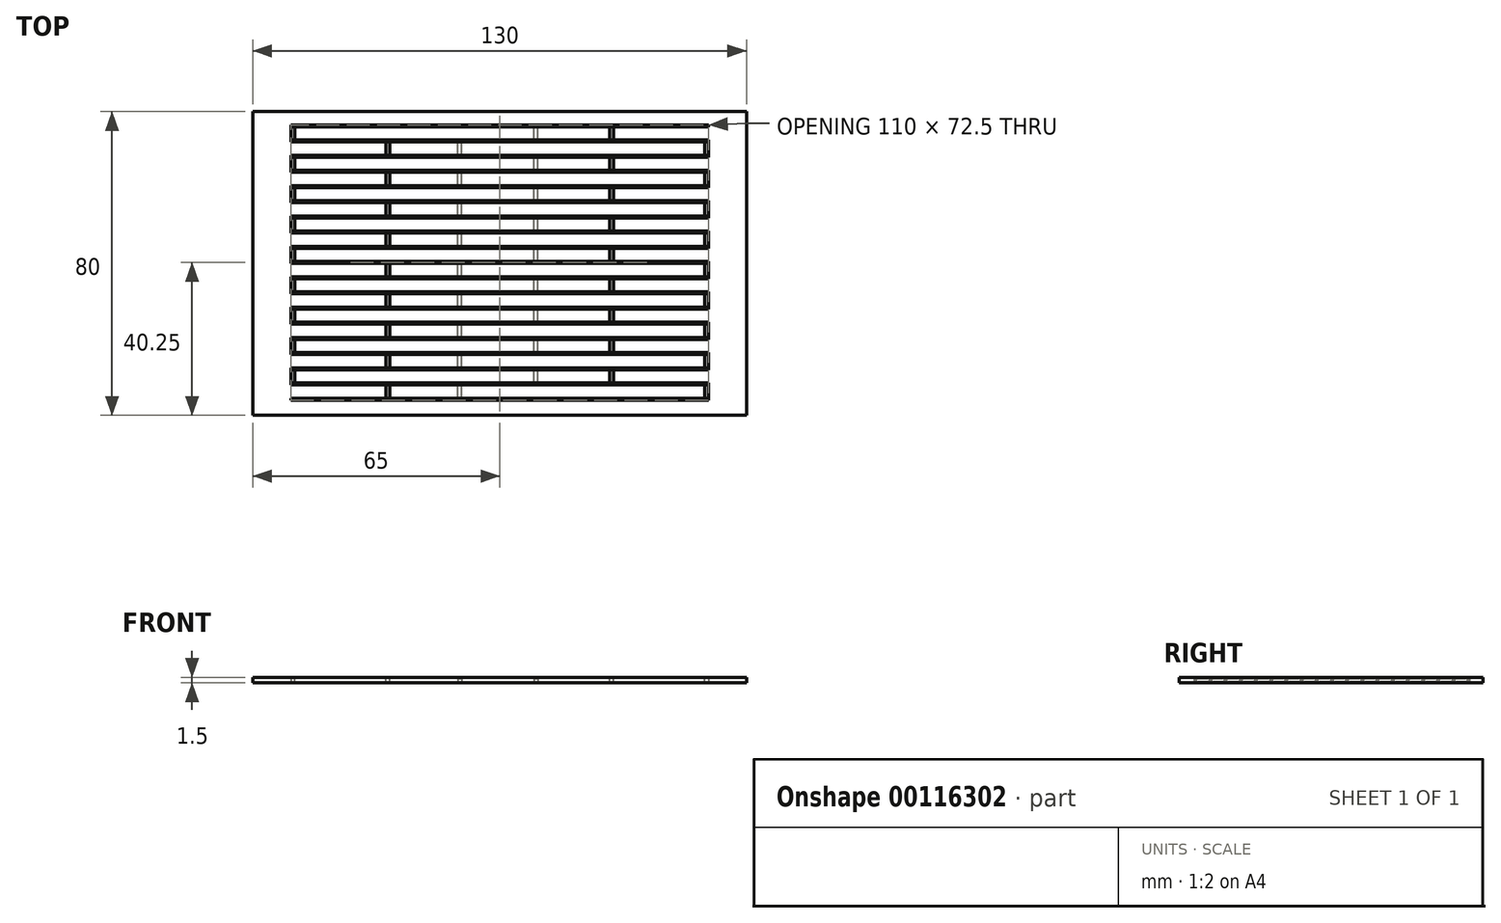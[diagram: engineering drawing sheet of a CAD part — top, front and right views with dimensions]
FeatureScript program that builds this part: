
annotation { "Feature Type Name" : "Feature", "Feature Type Description" : "" }
export const myFeature = defineFeature(function(context is Context, id is Id, definition is map)
    precondition{}
    {
        {
            var Q0;
            Q0=qCreatedBy(makeId("Top.planeOp"),FACE);
            var sketch = newSketch(context, id + "F0", { "sketchPlane" : qUnion([Q0])});
            skLineSegment(sketch, "E0.bottom", {"start": v(65, -40) * mm, "end": v(-65, -40) * mm});
            skLineSegment(sketch, "E0.top", {"start": v(65, 40) * mm, "end": v(-65, 40) * mm});
            skLineSegment(sketch, "E0.left", {"start": v(65, -40) * mm, "end": v(65, 40) * mm});
            skLineSegment(sketch, "E0.right", {"start": v(-65, -40) * mm, "end": v(-65, 40) * mm});
            skLineSegment(sketch, "E1", {"start": v(-55, 36.5) * mm, "end": v(-55, 36) * mm});
            skLineSegment(sketch, "E2.MirrorCS", {"start": v(55, 36.5) * mm, "end": v(55, 36) * mm});
            skLineSegment(sketch, "E3", {"start": v(-55, 36.5) * mm, "end": v(55, 36.5) * mm});
            skLineSegment(sketch, "E4", {"start": v(-55, 36) * mm, "end": v(55, 36) * mm});
            skLineSegment(sketch, "E5.0.1.0", {"start": v(-55, 32.5) * mm, "end": v(55, 32.5) * mm});
            skLineSegment(sketch, "E5.0.1.1", {"start": v(-55, 32) * mm, "end": v(55, 32) * mm});
            skLineSegment(sketch, "E5.0.2.0", {"start": v(-55, 28.5) * mm, "end": v(55, 28.5) * mm});
            skLineSegment(sketch, "E5.0.2.1", {"start": v(-55, 28) * mm, "end": v(55, 28) * mm});
            skLineSegment(sketch, "E5.0.3.0", {"start": v(-55, 24.5) * mm, "end": v(55, 24.5) * mm});
            skLineSegment(sketch, "E5.0.3.1", {"start": v(-55, 24) * mm, "end": v(55, 24) * mm});
            skLineSegment(sketch, "E5.0.4.0", {"start": v(-55, 20.5) * mm, "end": v(55, 20.5) * mm});
            skLineSegment(sketch, "E5.0.4.1", {"start": v(-55, 20) * mm, "end": v(55, 20) * mm});
            skLineSegment(sketch, "E5.0.5.0", {"start": v(-55, 16.5) * mm, "end": v(55, 16.5) * mm});
            skLineSegment(sketch, "E5.0.5.1", {"start": v(-55, 16) * mm, "end": v(55, 16) * mm});
            skLineSegment(sketch, "E5.0.6.0", {"start": v(-55, 12.5) * mm, "end": v(55, 12.5) * mm});
            skLineSegment(sketch, "E5.0.6.1", {"start": v(-55, 12) * mm, "end": v(55, 12) * mm});
            skLineSegment(sketch, "E5.0.7.0", {"start": v(-55, 8.5) * mm, "end": v(55, 8.5) * mm});
            skLineSegment(sketch, "E5.0.7.1", {"start": v(-55, 8) * mm, "end": v(55, 8) * mm});
            skLineSegment(sketch, "E5.0.8.0", {"start": v(-55, 4.5) * mm, "end": v(55, 4.5) * mm});
            skLineSegment(sketch, "E5.0.8.1", {"start": v(-55, 4) * mm, "end": v(55, 4) * mm});
            skLineSegment(sketch, "E5.0.9.0", {"start": v(-55, 0.5) * mm, "end": v(55, 0.5) * mm});
            skLineSegment(sketch, "E5.0.9.1", {"start": v(-55, 0) * mm, "end": v(55, 0) * mm});
            skLineSegment(sketch, "E5.0.10.0", {"start": v(-55, -3.5) * mm, "end": v(55, -3.5) * mm});
            skLineSegment(sketch, "E5.0.10.1", {"start": v(-55, -4) * mm, "end": v(55, -4) * mm});
            skLineSegment(sketch, "E5.0.11.0", {"start": v(-55, -7.5) * mm, "end": v(55, -7.5) * mm});
            skLineSegment(sketch, "E5.0.11.1", {"start": v(-55, -8) * mm, "end": v(55, -8) * mm});
            skLineSegment(sketch, "E5.0.12.0", {"start": v(-55, -11.5) * mm, "end": v(55, -11.5) * mm});
            skLineSegment(sketch, "E5.0.12.1", {"start": v(-55, -12) * mm, "end": v(55, -12) * mm});
            skLineSegment(sketch, "E5.0.13.0", {"start": v(-55, -15.5) * mm, "end": v(55, -15.5) * mm});
            skLineSegment(sketch, "E5.0.13.1", {"start": v(-55, -16) * mm, "end": v(55, -16) * mm});
            skLineSegment(sketch, "E5.0.14.0", {"start": v(-55, -19.5) * mm, "end": v(55, -19.5) * mm});
            skLineSegment(sketch, "E5.0.14.1", {"start": v(-55, -20) * mm, "end": v(55, -20) * mm});
            skLineSegment(sketch, "E5.0.15.0", {"start": v(-55, -23.5) * mm, "end": v(55, -23.5) * mm});
            skLineSegment(sketch, "E5.0.15.1", {"start": v(-55, -24) * mm, "end": v(55, -24) * mm});
            skLineSegment(sketch, "E5.0.16.0", {"start": v(-55, -27.5) * mm, "end": v(55, -27.5) * mm});
            skLineSegment(sketch, "E5.0.16.1", {"start": v(-55, -28) * mm, "end": v(55, -28) * mm});
            skLineSegment(sketch, "E5.0.17.0", {"start": v(-55, -31.5) * mm, "end": v(55, -31.5) * mm});
            skLineSegment(sketch, "E5.0.17.1", {"start": v(-55, -32) * mm, "end": v(55, -32) * mm});
            skLineSegment(sketch, "E5.0.18.0", {"start": v(-55, -35.5) * mm, "end": v(55, -35.5) * mm});
            skLineSegment(sketch, "E5.0.18.1", {"start": v(-55, -36) * mm, "end": v(55, -36) * mm});
            skLineSegment(sketch, "E5.direction1", {"start": v(-55, 36.5) * mm, "end": v(-12.48, 36.5) * mm, "construction": true});
            skLineSegment(sketch, "E5.direction2", {"start": v(-55, 36.5) * mm, "end": v(-55, 36) * mm, "construction": true});
            skPoint(sketch, "E6.orphan", {"position": v(-55, 40) * mm});
            skPoint(sketch, "E7.orphan", {"position": v(55, 40) * mm});
            skLineSegment(sketch, "E8.trimOffspring", {"start": v(55, 32.5) * mm, "end": v(55, 32) * mm});
            skLineSegment(sketch, "E9.trimOffspring", {"start": v(55, 28.5) * mm, "end": v(55, 28) * mm});
            skLineSegment(sketch, "E10.trimOffspring", {"start": v(55, 24.5) * mm, "end": v(55, 24) * mm});
            skLineSegment(sketch, "E11.trimOffspring", {"start": v(55, 20.5) * mm, "end": v(55, 20) * mm});
            skLineSegment(sketch, "E12.trimOffspring", {"start": v(55, 16.5) * mm, "end": v(55, 16) * mm});
            skLineSegment(sketch, "E13.trimOffspring", {"start": v(55, 12.5) * mm, "end": v(55, 12) * mm});
            skLineSegment(sketch, "E14.trimOffspring", {"start": v(55, 8.5) * mm, "end": v(55, 8) * mm});
            skLineSegment(sketch, "E15.trimOffspring", {"start": v(55, 4.5) * mm, "end": v(55, 4) * mm});
            skLineSegment(sketch, "E16.trimOffspring", {"start": v(55, 0.5) * mm, "end": v(55, 0) * mm});
            skLineSegment(sketch, "E17.trimOffspring", {"start": v(55, -3.5) * mm, "end": v(55, -4) * mm});
            skLineSegment(sketch, "E18.trimOffspring", {"start": v(55, -7.5) * mm, "end": v(55, -8) * mm});
            skLineSegment(sketch, "E19.trimOffspring", {"start": v(55, -11.5) * mm, "end": v(55, -12) * mm});
            skLineSegment(sketch, "E20.trimOffspring", {"start": v(55, -15.5) * mm, "end": v(55, -16) * mm});
            skLineSegment(sketch, "E21.trimOffspring", {"start": v(55, -19.5) * mm, "end": v(55, -20) * mm});
            skLineSegment(sketch, "E22.trimOffspring", {"start": v(55, -23.5) * mm, "end": v(55, -24) * mm});
            skLineSegment(sketch, "E23.trimOffspring", {"start": v(55, -27.5) * mm, "end": v(55, -28) * mm});
            skLineSegment(sketch, "E24.trimOffspring", {"start": v(55, -31.5) * mm, "end": v(55, -32) * mm});
            skLineSegment(sketch, "E25.trimOffspring", {"start": v(55, -35.5) * mm, "end": v(55, -36) * mm});
            skLineSegment(sketch, "E26.trimOffspring", {"start": v(-55, -31.5) * mm, "end": v(-55, -32) * mm});
            skLineSegment(sketch, "E27.trimOffspring", {"start": v(-55, -23.5) * mm, "end": v(-55, -24) * mm});
            skLineSegment(sketch, "E28.trimOffspring", {"start": v(-55, -15.5) * mm, "end": v(-55, -16) * mm});
            skLineSegment(sketch, "E29.trimOffspring", {"start": v(-55, -11.5) * mm, "end": v(-55, -12) * mm});
            skLineSegment(sketch, "E30.trimOffspring", {"start": v(-55, -7.5) * mm, "end": v(-55, -8) * mm});
            skLineSegment(sketch, "E31.trimOffspring", {"start": v(-55, -3.5) * mm, "end": v(-55, -4) * mm});
            skLineSegment(sketch, "E32.trimOffspring", {"start": v(-55, 0.5) * mm, "end": v(-55, 0) * mm});
            skLineSegment(sketch, "E33.trimOffspring", {"start": v(-55, 4.5) * mm, "end": v(-55, 4) * mm});
            skLineSegment(sketch, "E34.trimOffspring", {"start": v(-55, 8.5) * mm, "end": v(-55, 8) * mm});
            skLineSegment(sketch, "E35.trimOffspring", {"start": v(-55, 12.5) * mm, "end": v(-55, 12) * mm});
            skLineSegment(sketch, "E36.trimOffspring", {"start": v(-55, 16.5) * mm, "end": v(-55, 16) * mm});
            skLineSegment(sketch, "E37.trimOffspring", {"start": v(-55, -27.5) * mm, "end": v(-55, -28) * mm});
            skLineSegment(sketch, "E38.trimOffspring", {"start": v(-55, -19.5) * mm, "end": v(-55, -20) * mm});
            skLineSegment(sketch, "E39.trimOffspring", {"start": v(-55, -35.5) * mm, "end": v(-55, -36) * mm});
            skPoint(sketch, "E40.orphan", {"position": v(-55, -40) * mm});
            skLineSegment(sketch, "E41.trimOffspring", {"start": v(-55, 24.5) * mm, "end": v(-55, 24) * mm});
            skLineSegment(sketch, "E42.trimOffspring", {"start": v(-55, 20.5) * mm, "end": v(-55, 20) * mm});
            skLineSegment(sketch, "E43.trimOffspring", {"start": v(-55, 32.5) * mm, "end": v(-55, 32) * mm});
            skPoint(sketch, "E44.orphan", {"position": v(55, -40) * mm});
            skLineSegment(sketch, "E45", {"start": v(-55, 28.5) * mm, "end": v(-55, 28) * mm});
            skSolve(sketch);
        }
        {
            var Q0;
            Q0 = qSketchRegion(id + "F0", true);
            extrude(context, id + "F1", {"entities" : qUnion([Q0]), "depth" : 1.5 * mm});
        }
        {
            var Q0;
            Q0=makeQuery(id+"F1.opExtrude","CAP_FACE",FACE,{"disambiguationData":[OSD([sQuery(id+"F0.wireOp",EDGE,"E0.bottom"),sQuery(id+"F0.wireOp",EDGE,"E0.top"),sQuery(id+"F0.wireOp",EDGE,"E0.left"),sQuery(id+"F0.wireOp",EDGE,"E0.right"),sQuery(id+"F0.wireOp",EDGE,"E1"),sQuery(id+"F0.wireOp",EDGE,"E2.MirrorCS"),sQuery(id+"F0.wireOp",EDGE,"E3"),sQuery(id+"F0.wireOp",EDGE,"E4"),sQuery(id+"F0.wireOp",EDGE,"E5.0.1.0"),sQuery(id+"F0.wireOp",EDGE,"E5.0.1.1"),sQuery(id+"F0.wireOp",EDGE,"E5.0.2.0"),sQuery(id+"F0.wireOp",EDGE,"E5.0.2.1"),sQuery(id+"F0.wireOp",EDGE,"E5.0.3.0"),sQuery(id+"F0.wireOp",EDGE,"E5.0.3.1"),sQuery(id+"F0.wireOp",EDGE,"E5.0.4.0"),sQuery(id+"F0.wireOp",EDGE,"E5.0.4.1"),sQuery(id+"F0.wireOp",EDGE,"E5.0.5.0"),sQuery(id+"F0.wireOp",EDGE,"E5.0.5.1"),sQuery(id+"F0.wireOp",EDGE,"E5.0.6.0"),sQuery(id+"F0.wireOp",EDGE,"E5.0.6.1"),sQuery(id+"F0.wireOp",EDGE,"E5.0.7.0"),sQuery(id+"F0.wireOp",EDGE,"E5.0.7.1"),sQuery(id+"F0.wireOp",EDGE,"E5.0.8.0"),sQuery(id+"F0.wireOp",EDGE,"E5.0.8.1"),sQuery(id+"F0.wireOp",EDGE,"E5.0.9.0"),sQuery(id+"F0.wireOp",EDGE,"E5.0.9.1"),sQuery(id+"F0.wireOp",EDGE,"E5.0.10.0"),sQuery(id+"F0.wireOp",EDGE,"E5.0.10.1"),sQuery(id+"F0.wireOp",EDGE,"E5.0.11.0"),sQuery(id+"F0.wireOp",EDGE,"E5.0.11.1"),sQuery(id+"F0.wireOp",EDGE,"E5.0.12.0"),sQuery(id+"F0.wireOp",EDGE,"E5.0.12.1"),sQuery(id+"F0.wireOp",EDGE,"E5.0.13.0"),sQuery(id+"F0.wireOp",EDGE,"E5.0.13.1"),sQuery(id+"F0.wireOp",EDGE,"E5.0.14.0"),sQuery(id+"F0.wireOp",EDGE,"E5.0.14.1"),sQuery(id+"F0.wireOp",EDGE,"E5.0.15.0"),sQuery(id+"F0.wireOp",EDGE,"E5.0.15.1"),sQuery(id+"F0.wireOp",EDGE,"E5.0.16.0"),sQuery(id+"F0.wireOp",EDGE,"E5.0.16.1"),sQuery(id+"F0.wireOp",EDGE,"E5.0.17.0"),sQuery(id+"F0.wireOp",EDGE,"E5.0.17.1"),sQuery(id+"F0.wireOp",EDGE,"E5.0.18.0"),sQuery(id+"F0.wireOp",EDGE,"E5.0.18.1"),sQuery(id+"F0.wireOp",EDGE,"E8.trimOffspring"),sQuery(id+"F0.wireOp",EDGE,"E9.trimOffspring"),sQuery(id+"F0.wireOp",EDGE,"E10.trimOffspring"),sQuery(id+"F0.wireOp",EDGE,"E11.trimOffspring"),sQuery(id+"F0.wireOp",EDGE,"E12.trimOffspring"),sQuery(id+"F0.wireOp",EDGE,"E13.trimOffspring"),sQuery(id+"F0.wireOp",EDGE,"E14.trimOffspring"),sQuery(id+"F0.wireOp",EDGE,"E15.trimOffspring"),sQuery(id+"F0.wireOp",EDGE,"E16.trimOffspring"),sQuery(id+"F0.wireOp",EDGE,"E17.trimOffspring"),sQuery(id+"F0.wireOp",EDGE,"E18.trimOffspring"),sQuery(id+"F0.wireOp",EDGE,"E19.trimOffspring"),sQuery(id+"F0.wireOp",EDGE,"E20.trimOffspring"),sQuery(id+"F0.wireOp",EDGE,"E21.trimOffspring"),sQuery(id+"F0.wireOp",EDGE,"E22.trimOffspring"),sQuery(id+"F0.wireOp",EDGE,"E23.trimOffspring"),sQuery(id+"F0.wireOp",EDGE,"E24.trimOffspring"),sQuery(id+"F0.wireOp",EDGE,"E25.trimOffspring"),sQuery(id+"F0.wireOp",EDGE,"E26.trimOffspring"),sQuery(id+"F0.wireOp",EDGE,"E27.trimOffspring"),sQuery(id+"F0.wireOp",EDGE,"E28.trimOffspring"),sQuery(id+"F0.wireOp",EDGE,"E29.trimOffspring"),sQuery(id+"F0.wireOp",EDGE,"E30.trimOffspring"),sQuery(id+"F0.wireOp",EDGE,"E31.trimOffspring"),sQuery(id+"F0.wireOp",EDGE,"E32.trimOffspring"),sQuery(id+"F0.wireOp",EDGE,"E33.trimOffspring"),sQuery(id+"F0.wireOp",EDGE,"E34.trimOffspring"),sQuery(id+"F0.wireOp",EDGE,"E35.trimOffspring"),sQuery(id+"F0.wireOp",EDGE,"E36.trimOffspring"),sQuery(id+"F0.wireOp",EDGE,"E37.trimOffspring"),sQuery(id+"F0.wireOp",EDGE,"E38.trimOffspring"),sQuery(id+"F0.wireOp",EDGE,"E39.trimOffspring"),sQuery(id+"F0.wireOp",EDGE,"E41.trimOffspring"),sQuery(id+"F0.wireOp",EDGE,"E42.trimOffspring"),sQuery(id+"F0.wireOp",EDGE,"E43.trimOffspring"),sQuery(id+"F0.wireOp",EDGE,"E45")])],"isStart":false});
            var sketch = newSketch(context, id + "F2", { "sketchPlane" : qUnion([Q0])});
            skLineSegment(sketch, "E46.bottom", {"start": v(-55, 36.5) * mm, "end": v(-54, 36.5) * mm});
            skLineSegment(sketch, "E46.top", {"start": v(-55, 32) * mm, "end": v(-54, 32) * mm});
            skLineSegment(sketch, "E46.left", {"start": v(-55, 36.5) * mm, "end": v(-55, 32) * mm});
            skLineSegment(sketch, "E46.right", {"start": v(-54, 36.5) * mm, "end": v(-54, 32) * mm});
            skLineSegment(sketch, "E47.bottom", {"start": v(55, 32.5) * mm, "end": v(54, 32.5) * mm});
            skLineSegment(sketch, "E47.top", {"start": v(55, 28) * mm, "end": v(54, 28) * mm});
            skLineSegment(sketch, "E47.left", {"start": v(55, 32.5) * mm, "end": v(55, 28) * mm});
            skLineSegment(sketch, "E47.right", {"start": v(54, 32.5) * mm, "end": v(54, 28) * mm});
            skLineSegment(sketch, "E48.0.1.0", {"start": v(54, 24.5) * mm, "end": v(54, 20) * mm});
            skLineSegment(sketch, "E48.0.1.1", {"start": v(55, 24.5) * mm, "end": v(55, 20) * mm});
            skLineSegment(sketch, "E48.0.1.2", {"start": v(55, 20) * mm, "end": v(54, 20) * mm});
            skLineSegment(sketch, "E48.0.1.3", {"start": v(55, 24.5) * mm, "end": v(54, 24.5) * mm});
            skLineSegment(sketch, "E48.0.2.0", {"start": v(54, 16.5) * mm, "end": v(54, 12) * mm});
            skLineSegment(sketch, "E48.0.2.1", {"start": v(55, 16.5) * mm, "end": v(55, 12) * mm});
            skLineSegment(sketch, "E48.0.2.2", {"start": v(55, 12) * mm, "end": v(54, 12) * mm});
            skLineSegment(sketch, "E48.0.2.3", {"start": v(55, 16.5) * mm, "end": v(54, 16.5) * mm});
            skLineSegment(sketch, "E48.0.3.0", {"start": v(54, 8.5) * mm, "end": v(54, 4) * mm});
            skLineSegment(sketch, "E48.0.3.1", {"start": v(55, 8.5) * mm, "end": v(55, 4) * mm});
            skLineSegment(sketch, "E48.0.3.2", {"start": v(55, 4) * mm, "end": v(54, 4) * mm});
            skLineSegment(sketch, "E48.0.3.3", {"start": v(55, 8.5) * mm, "end": v(54, 8.5) * mm});
            skLineSegment(sketch, "E48.0.4.0", {"start": v(54, 0.5) * mm, "end": v(54, -4) * mm});
            skLineSegment(sketch, "E48.0.4.1", {"start": v(55, 0.5) * mm, "end": v(55, -4) * mm});
            skLineSegment(sketch, "E48.0.4.2", {"start": v(55, -4) * mm, "end": v(54, -4) * mm});
            skLineSegment(sketch, "E48.0.4.3", {"start": v(55, 0.5) * mm, "end": v(54, 0.5) * mm});
            skLineSegment(sketch, "E48.0.5.0", {"start": v(54, -7.5) * mm, "end": v(54, -12) * mm});
            skLineSegment(sketch, "E48.0.5.1", {"start": v(55, -7.5) * mm, "end": v(55, -12) * mm});
            skLineSegment(sketch, "E48.0.5.2", {"start": v(55, -12) * mm, "end": v(54, -12) * mm});
            skLineSegment(sketch, "E48.0.5.3", {"start": v(55, -7.5) * mm, "end": v(54, -7.5) * mm});
            skLineSegment(sketch, "E48.0.6.0", {"start": v(54, -15.5) * mm, "end": v(54, -20) * mm});
            skLineSegment(sketch, "E48.0.6.1", {"start": v(55, -15.5) * mm, "end": v(55, -20) * mm});
            skLineSegment(sketch, "E48.0.6.2", {"start": v(55, -20) * mm, "end": v(54, -20) * mm});
            skLineSegment(sketch, "E48.0.6.3", {"start": v(55, -15.5) * mm, "end": v(54, -15.5) * mm});
            skLineSegment(sketch, "E48.0.7.0", {"start": v(54, -23.5) * mm, "end": v(54, -28) * mm});
            skLineSegment(sketch, "E48.0.7.1", {"start": v(55, -23.5) * mm, "end": v(55, -28) * mm});
            skLineSegment(sketch, "E48.0.7.2", {"start": v(55, -28) * mm, "end": v(54, -28) * mm});
            skLineSegment(sketch, "E48.0.7.3", {"start": v(55, -23.5) * mm, "end": v(54, -23.5) * mm});
            skLineSegment(sketch, "E48.0.8.0", {"start": v(54, -31.5) * mm, "end": v(54, -36) * mm});
            skLineSegment(sketch, "E48.0.8.1", {"start": v(55, -31.5) * mm, "end": v(55, -36) * mm});
            skLineSegment(sketch, "E48.0.8.2", {"start": v(55, -36) * mm, "end": v(54, -36) * mm});
            skLineSegment(sketch, "E48.0.8.3", {"start": v(55, -31.5) * mm, "end": v(54, -31.5) * mm});
            skLineSegment(sketch, "E48.direction1", {"start": v(54, 28) * mm, "end": v(79, 28) * mm, "construction": true});
            skLineSegment(sketch, "E48.direction2", {"start": v(54, 28) * mm, "end": v(54, 20) * mm, "construction": true});
            skLineSegment(sketch, "E49.0.1.0", {"start": v(-55, 28.5) * mm, "end": v(-55, 24) * mm});
            skLineSegment(sketch, "E49.0.1.1", {"start": v(-54, 28.5) * mm, "end": v(-54, 24) * mm});
            skLineSegment(sketch, "E49.0.1.2", {"start": v(-55, 28.5) * mm, "end": v(-54, 28.5) * mm});
            skLineSegment(sketch, "E49.0.1.3", {"start": v(-55, 24) * mm, "end": v(-54, 24) * mm});
            skLineSegment(sketch, "E49.0.2.0", {"start": v(-55, 20.5) * mm, "end": v(-55, 16) * mm});
            skLineSegment(sketch, "E49.0.2.1", {"start": v(-54, 20.5) * mm, "end": v(-54, 16) * mm});
            skLineSegment(sketch, "E49.0.2.2", {"start": v(-55, 20.5) * mm, "end": v(-54, 20.5) * mm});
            skLineSegment(sketch, "E49.0.2.3", {"start": v(-55, 16) * mm, "end": v(-54, 16) * mm});
            skLineSegment(sketch, "E49.0.3.0", {"start": v(-55, 12.5) * mm, "end": v(-55, 8) * mm});
            skLineSegment(sketch, "E49.0.3.1", {"start": v(-54, 12.5) * mm, "end": v(-54, 8) * mm});
            skLineSegment(sketch, "E49.0.3.2", {"start": v(-55, 12.5) * mm, "end": v(-54, 12.5) * mm});
            skLineSegment(sketch, "E49.0.3.3", {"start": v(-55, 8) * mm, "end": v(-54, 8) * mm});
            skLineSegment(sketch, "E49.0.4.0", {"start": v(-55, 4.5) * mm, "end": v(-55, 0) * mm});
            skLineSegment(sketch, "E49.0.4.1", {"start": v(-54, 4.5) * mm, "end": v(-54, 0) * mm});
            skLineSegment(sketch, "E49.0.4.2", {"start": v(-55, 4.5) * mm, "end": v(-54, 4.5) * mm});
            skLineSegment(sketch, "E49.0.4.3", {"start": v(-55, 0) * mm, "end": v(-54, 0) * mm});
            skLineSegment(sketch, "E49.0.5.0", {"start": v(-55, -3.5) * mm, "end": v(-55, -8) * mm});
            skLineSegment(sketch, "E49.0.5.1", {"start": v(-54, -3.5) * mm, "end": v(-54, -8) * mm});
            skLineSegment(sketch, "E49.0.5.2", {"start": v(-55, -3.5) * mm, "end": v(-54, -3.5) * mm});
            skLineSegment(sketch, "E49.0.5.3", {"start": v(-55, -8) * mm, "end": v(-54, -8) * mm});
            skLineSegment(sketch, "E49.0.6.0", {"start": v(-55, -11.5) * mm, "end": v(-55, -16) * mm});
            skLineSegment(sketch, "E49.0.6.1", {"start": v(-54, -11.5) * mm, "end": v(-54, -16) * mm});
            skLineSegment(sketch, "E49.0.6.2", {"start": v(-55, -11.5) * mm, "end": v(-54, -11.5) * mm});
            skLineSegment(sketch, "E49.0.6.3", {"start": v(-55, -16) * mm, "end": v(-54, -16) * mm});
            skLineSegment(sketch, "E49.0.7.0", {"start": v(-55, -19.5) * mm, "end": v(-55, -24) * mm});
            skLineSegment(sketch, "E49.0.7.1", {"start": v(-54, -19.5) * mm, "end": v(-54, -24) * mm});
            skLineSegment(sketch, "E49.0.7.2", {"start": v(-55, -19.5) * mm, "end": v(-54, -19.5) * mm});
            skLineSegment(sketch, "E49.0.7.3", {"start": v(-55, -24) * mm, "end": v(-54, -24) * mm});
            skLineSegment(sketch, "E49.0.8.0", {"start": v(-55, -27.5) * mm, "end": v(-55, -32) * mm});
            skLineSegment(sketch, "E49.0.8.1", {"start": v(-54, -27.5) * mm, "end": v(-54, -32) * mm});
            skLineSegment(sketch, "E49.0.8.2", {"start": v(-55, -27.5) * mm, "end": v(-54, -27.5) * mm});
            skLineSegment(sketch, "E49.0.8.3", {"start": v(-55, -32) * mm, "end": v(-54, -32) * mm});
            skLineSegment(sketch, "E49.direction1", {"start": v(-55, 32) * mm, "end": v(-30, 32) * mm, "construction": true});
            skLineSegment(sketch, "E49.direction2", {"start": v(-55, 32) * mm, "end": v(-55, 24) * mm, "construction": true});
            skSolve(sketch);
        }
        {
            var Q0;
            Q0 = qSketchRegion(id + "F2", true);
            extrude(context, id + "F3", {"entities" : qUnion([Q0]), "operationType" : NewBodyOperationType.REMOVE, "oppositeDirection" : true, "depth" : 1.2 * mm});
        }
        {
            var Q0;
            Q0=makeQuery(id+"F1.opExtrude","CAP_FACE",FACE,{"disambiguationData":[OSD([sQuery(id+"F0.wireOp",EDGE,"E0.bottom"),sQuery(id+"F0.wireOp",EDGE,"E0.top"),sQuery(id+"F0.wireOp",EDGE,"E0.left"),sQuery(id+"F0.wireOp",EDGE,"E0.right"),sQuery(id+"F0.wireOp",EDGE,"E1"),sQuery(id+"F0.wireOp",EDGE,"E2.MirrorCS"),sQuery(id+"F0.wireOp",EDGE,"E3"),sQuery(id+"F0.wireOp",EDGE,"E4"),sQuery(id+"F0.wireOp",EDGE,"E5.0.1.0"),sQuery(id+"F0.wireOp",EDGE,"E5.0.1.1"),sQuery(id+"F0.wireOp",EDGE,"E5.0.2.0"),sQuery(id+"F0.wireOp",EDGE,"E5.0.2.1"),sQuery(id+"F0.wireOp",EDGE,"E5.0.3.0"),sQuery(id+"F0.wireOp",EDGE,"E5.0.3.1"),sQuery(id+"F0.wireOp",EDGE,"E5.0.4.0"),sQuery(id+"F0.wireOp",EDGE,"E5.0.4.1"),sQuery(id+"F0.wireOp",EDGE,"E5.0.5.0"),sQuery(id+"F0.wireOp",EDGE,"E5.0.5.1"),sQuery(id+"F0.wireOp",EDGE,"E5.0.6.0"),sQuery(id+"F0.wireOp",EDGE,"E5.0.6.1"),sQuery(id+"F0.wireOp",EDGE,"E5.0.7.0"),sQuery(id+"F0.wireOp",EDGE,"E5.0.7.1"),sQuery(id+"F0.wireOp",EDGE,"E5.0.8.0"),sQuery(id+"F0.wireOp",EDGE,"E5.0.8.1"),sQuery(id+"F0.wireOp",EDGE,"E5.0.9.0"),sQuery(id+"F0.wireOp",EDGE,"E5.0.9.1"),sQuery(id+"F0.wireOp",EDGE,"E5.0.10.0"),sQuery(id+"F0.wireOp",EDGE,"E5.0.10.1"),sQuery(id+"F0.wireOp",EDGE,"E5.0.11.0"),sQuery(id+"F0.wireOp",EDGE,"E5.0.11.1"),sQuery(id+"F0.wireOp",EDGE,"E5.0.12.0"),sQuery(id+"F0.wireOp",EDGE,"E5.0.12.1"),sQuery(id+"F0.wireOp",EDGE,"E5.0.13.0"),sQuery(id+"F0.wireOp",EDGE,"E5.0.13.1"),sQuery(id+"F0.wireOp",EDGE,"E5.0.14.0"),sQuery(id+"F0.wireOp",EDGE,"E5.0.14.1"),sQuery(id+"F0.wireOp",EDGE,"E5.0.15.0"),sQuery(id+"F0.wireOp",EDGE,"E5.0.15.1"),sQuery(id+"F0.wireOp",EDGE,"E5.0.16.0"),sQuery(id+"F0.wireOp",EDGE,"E5.0.16.1"),sQuery(id+"F0.wireOp",EDGE,"E5.0.17.0"),sQuery(id+"F0.wireOp",EDGE,"E5.0.17.1"),sQuery(id+"F0.wireOp",EDGE,"E5.0.18.0"),sQuery(id+"F0.wireOp",EDGE,"E5.0.18.1"),sQuery(id+"F0.wireOp",EDGE,"E8.trimOffspring"),sQuery(id+"F0.wireOp",EDGE,"E9.trimOffspring"),sQuery(id+"F0.wireOp",EDGE,"E10.trimOffspring"),sQuery(id+"F0.wireOp",EDGE,"E11.trimOffspring"),sQuery(id+"F0.wireOp",EDGE,"E12.trimOffspring"),sQuery(id+"F0.wireOp",EDGE,"E13.trimOffspring"),sQuery(id+"F0.wireOp",EDGE,"E14.trimOffspring"),sQuery(id+"F0.wireOp",EDGE,"E15.trimOffspring"),sQuery(id+"F0.wireOp",EDGE,"E16.trimOffspring"),sQuery(id+"F0.wireOp",EDGE,"E17.trimOffspring"),sQuery(id+"F0.wireOp",EDGE,"E18.trimOffspring"),sQuery(id+"F0.wireOp",EDGE,"E19.trimOffspring"),sQuery(id+"F0.wireOp",EDGE,"E20.trimOffspring"),sQuery(id+"F0.wireOp",EDGE,"E21.trimOffspring"),sQuery(id+"F0.wireOp",EDGE,"E22.trimOffspring"),sQuery(id+"F0.wireOp",EDGE,"E23.trimOffspring"),sQuery(id+"F0.wireOp",EDGE,"E24.trimOffspring"),sQuery(id+"F0.wireOp",EDGE,"E25.trimOffspring"),sQuery(id+"F0.wireOp",EDGE,"E26.trimOffspring"),sQuery(id+"F0.wireOp",EDGE,"E27.trimOffspring"),sQuery(id+"F0.wireOp",EDGE,"E28.trimOffspring"),sQuery(id+"F0.wireOp",EDGE,"E29.trimOffspring"),sQuery(id+"F0.wireOp",EDGE,"E30.trimOffspring"),sQuery(id+"F0.wireOp",EDGE,"E31.trimOffspring"),sQuery(id+"F0.wireOp",EDGE,"E32.trimOffspring"),sQuery(id+"F0.wireOp",EDGE,"E33.trimOffspring"),sQuery(id+"F0.wireOp",EDGE,"E34.trimOffspring"),sQuery(id+"F0.wireOp",EDGE,"E35.trimOffspring"),sQuery(id+"F0.wireOp",EDGE,"E36.trimOffspring"),sQuery(id+"F0.wireOp",EDGE,"E37.trimOffspring"),sQuery(id+"F0.wireOp",EDGE,"E38.trimOffspring"),sQuery(id+"F0.wireOp",EDGE,"E39.trimOffspring"),sQuery(id+"F0.wireOp",EDGE,"E41.trimOffspring"),sQuery(id+"F0.wireOp",EDGE,"E42.trimOffspring"),sQuery(id+"F0.wireOp",EDGE,"E43.trimOffspring"),sQuery(id+"F0.wireOp",EDGE,"E45")])],"isStart":false});
            var sketch = newSketch(context, id + "F4", { "sketchPlane" : qUnion([Q0])});
            skLineSegment(sketch, "E50.bottom", {"start": v(29, 36) * mm, "end": v(30, 36) * mm});
            skLineSegment(sketch, "E50.top", {"start": v(29, 32.5) * mm, "end": v(30, 32.5) * mm});
            skLineSegment(sketch, "E50.left", {"start": v(29, 36) * mm, "end": v(29, 32.5) * mm});
            skLineSegment(sketch, "E50.right", {"start": v(30, 36) * mm, "end": v(30, 32.5) * mm});
            skLineSegment(sketch, "E51.bottom", {"start": v(-30, 32) * mm, "end": v(-29, 32) * mm});
            skLineSegment(sketch, "E51.top", {"start": v(-30, 28) * mm, "end": v(-29, 28) * mm});
            skLineSegment(sketch, "E51.left", {"start": v(-30, 32) * mm, "end": v(-30, 28) * mm});
            skLineSegment(sketch, "E51.right", {"start": v(-29, 32) * mm, "end": v(-29, 28) * mm});
            skLineSegment(sketch, "E52.0.1.0", {"start": v(-30, 24) * mm, "end": v(-30, 20) * mm});
            skLineSegment(sketch, "E52.0.1.1", {"start": v(-29, 24) * mm, "end": v(-29, 20) * mm});
            skLineSegment(sketch, "E52.0.1.2", {"start": v(-30, 20) * mm, "end": v(-29, 20) * mm});
            skLineSegment(sketch, "E52.0.1.3", {"start": v(-30, 24) * mm, "end": v(-29, 24) * mm});
            skLineSegment(sketch, "E52.0.1.4", {"start": v(30, 28) * mm, "end": v(30, 24.5) * mm});
            skLineSegment(sketch, "E52.0.1.5", {"start": v(29, 28) * mm, "end": v(29, 24.5) * mm});
            skLineSegment(sketch, "E52.0.1.6", {"start": v(29, 24.5) * mm, "end": v(30, 24.5) * mm});
            skLineSegment(sketch, "E52.0.1.7", {"start": v(29, 28) * mm, "end": v(30, 28) * mm});
            skLineSegment(sketch, "E52.0.2.0", {"start": v(-30, 16) * mm, "end": v(-30, 12) * mm});
            skLineSegment(sketch, "E52.0.2.1", {"start": v(-29, 16) * mm, "end": v(-29, 12) * mm});
            skLineSegment(sketch, "E52.0.2.2", {"start": v(-30, 12) * mm, "end": v(-29, 12) * mm});
            skLineSegment(sketch, "E52.0.2.3", {"start": v(-30, 16) * mm, "end": v(-29, 16) * mm});
            skLineSegment(sketch, "E52.0.2.4", {"start": v(30, 20) * mm, "end": v(30, 16.5) * mm});
            skLineSegment(sketch, "E52.0.2.5", {"start": v(29, 20) * mm, "end": v(29, 16.5) * mm});
            skLineSegment(sketch, "E52.0.2.6", {"start": v(29, 16.5) * mm, "end": v(30, 16.5) * mm});
            skLineSegment(sketch, "E52.0.2.7", {"start": v(29, 20) * mm, "end": v(30, 20) * mm});
            skLineSegment(sketch, "E52.0.3.0", {"start": v(-30, 8) * mm, "end": v(-30, 4) * mm});
            skLineSegment(sketch, "E52.0.3.1", {"start": v(-29, 8) * mm, "end": v(-29, 4) * mm});
            skLineSegment(sketch, "E52.0.3.2", {"start": v(-30, 4) * mm, "end": v(-29, 4) * mm});
            skLineSegment(sketch, "E52.0.3.3", {"start": v(-30, 8) * mm, "end": v(-29, 8) * mm});
            skLineSegment(sketch, "E52.0.3.4", {"start": v(30, 12) * mm, "end": v(30, 8.5) * mm});
            skLineSegment(sketch, "E52.0.3.5", {"start": v(29, 12) * mm, "end": v(29, 8.5) * mm});
            skLineSegment(sketch, "E52.0.3.6", {"start": v(29, 8.5) * mm, "end": v(30, 8.5) * mm});
            skLineSegment(sketch, "E52.0.3.7", {"start": v(29, 12) * mm, "end": v(30, 12) * mm});
            skLineSegment(sketch, "E52.0.4.0", {"start": v(-30, 0) * mm, "end": v(-30, -4) * mm});
            skLineSegment(sketch, "E52.0.4.1", {"start": v(-29, 0) * mm, "end": v(-29, -4) * mm});
            skLineSegment(sketch, "E52.0.4.2", {"start": v(-30, -4) * mm, "end": v(-29, -4) * mm});
            skLineSegment(sketch, "E52.0.4.3", {"start": v(-30, 0) * mm, "end": v(-29, 0) * mm});
            skLineSegment(sketch, "E52.0.4.4", {"start": v(30, 4) * mm, "end": v(30, 0.5) * mm});
            skLineSegment(sketch, "E52.0.4.5", {"start": v(29, 4) * mm, "end": v(29, 0.5) * mm});
            skLineSegment(sketch, "E52.0.4.6", {"start": v(29, 0.5) * mm, "end": v(30, 0.5) * mm});
            skLineSegment(sketch, "E52.0.4.7", {"start": v(29, 4) * mm, "end": v(30, 4) * mm});
            skLineSegment(sketch, "E52.0.5.0", {"start": v(-30, -8) * mm, "end": v(-30, -12) * mm});
            skLineSegment(sketch, "E52.0.5.1", {"start": v(-29, -8) * mm, "end": v(-29, -12) * mm});
            skLineSegment(sketch, "E52.0.5.2", {"start": v(-30, -12) * mm, "end": v(-29, -12) * mm});
            skLineSegment(sketch, "E52.0.5.3", {"start": v(-30, -8) * mm, "end": v(-29, -8) * mm});
            skLineSegment(sketch, "E52.0.5.4", {"start": v(30, -4) * mm, "end": v(30, -7.5) * mm});
            skLineSegment(sketch, "E52.0.5.5", {"start": v(29, -4) * mm, "end": v(29, -7.5) * mm});
            skLineSegment(sketch, "E52.0.5.6", {"start": v(29, -7.5) * mm, "end": v(30, -7.5) * mm});
            skLineSegment(sketch, "E52.0.5.7", {"start": v(29, -4) * mm, "end": v(30, -4) * mm});
            skLineSegment(sketch, "E52.0.6.0", {"start": v(-30, -16) * mm, "end": v(-30, -20) * mm});
            skLineSegment(sketch, "E52.0.6.1", {"start": v(-29, -16) * mm, "end": v(-29, -20) * mm});
            skLineSegment(sketch, "E52.0.6.2", {"start": v(-30, -20) * mm, "end": v(-29, -20) * mm});
            skLineSegment(sketch, "E52.0.6.3", {"start": v(-30, -16) * mm, "end": v(-29, -16) * mm});
            skLineSegment(sketch, "E52.0.6.4", {"start": v(30, -12) * mm, "end": v(30, -15.5) * mm});
            skLineSegment(sketch, "E52.0.6.5", {"start": v(29, -12) * mm, "end": v(29, -15.5) * mm});
            skLineSegment(sketch, "E52.0.6.6", {"start": v(29, -15.5) * mm, "end": v(30, -15.5) * mm});
            skLineSegment(sketch, "E52.0.6.7", {"start": v(29, -12) * mm, "end": v(30, -12) * mm});
            skLineSegment(sketch, "E52.0.7.0", {"start": v(-30, -24) * mm, "end": v(-30, -28) * mm});
            skLineSegment(sketch, "E52.0.7.1", {"start": v(-29, -24) * mm, "end": v(-29, -28) * mm});
            skLineSegment(sketch, "E52.0.7.2", {"start": v(-30, -28) * mm, "end": v(-29, -28) * mm});
            skLineSegment(sketch, "E52.0.7.3", {"start": v(-30, -24) * mm, "end": v(-29, -24) * mm});
            skLineSegment(sketch, "E52.0.7.4", {"start": v(30, -20) * mm, "end": v(30, -23.5) * mm});
            skLineSegment(sketch, "E52.0.7.5", {"start": v(29, -20) * mm, "end": v(29, -23.5) * mm});
            skLineSegment(sketch, "E52.0.7.6", {"start": v(29, -23.5) * mm, "end": v(30, -23.5) * mm});
            skLineSegment(sketch, "E52.0.7.7", {"start": v(29, -20) * mm, "end": v(30, -20) * mm});
            skLineSegment(sketch, "E52.0.8.0", {"start": v(-30, -32) * mm, "end": v(-30, -36) * mm});
            skLineSegment(sketch, "E52.0.8.1", {"start": v(-29, -32) * mm, "end": v(-29, -36) * mm});
            skLineSegment(sketch, "E52.0.8.2", {"start": v(-30, -36) * mm, "end": v(-29, -36) * mm});
            skLineSegment(sketch, "E52.0.8.3", {"start": v(-30, -32) * mm, "end": v(-29, -32) * mm});
            skLineSegment(sketch, "E52.0.8.4", {"start": v(30, -28) * mm, "end": v(30, -31.5) * mm});
            skLineSegment(sketch, "E52.0.8.5", {"start": v(29, -28) * mm, "end": v(29, -31.5) * mm});
            skLineSegment(sketch, "E52.0.8.6", {"start": v(29, -31.5) * mm, "end": v(30, -31.5) * mm});
            skLineSegment(sketch, "E52.0.8.7", {"start": v(29, -28) * mm, "end": v(30, -28) * mm});
            skLineSegment(sketch, "E52.direction1", {"start": v(-30, 28) * mm, "end": v(-5, 28) * mm, "construction": true});
            skLineSegment(sketch, "E52.direction2", {"start": v(-30, 28) * mm, "end": v(-30, 20) * mm, "construction": true});
            skSolve(sketch);
        }
        {
            var Q0;
            Q0 = qSketchRegion(id + "F4", true);
            extrude(context, id + "F5", {"entities" : qUnion([Q0]), "operationType" : NewBodyOperationType.REMOVE, "oppositeDirection" : true, "depth" : 1.2 * mm});
        }
        {
            var Q0;
            Q0=makeQuery(id+"F1.opExtrude","CAP_FACE",FACE,{"disambiguationData":[OSD([sQuery(id+"F0.wireOp",EDGE,"E0.bottom"),sQuery(id+"F0.wireOp",EDGE,"E0.top"),sQuery(id+"F0.wireOp",EDGE,"E0.left"),sQuery(id+"F0.wireOp",EDGE,"E0.right"),sQuery(id+"F0.wireOp",EDGE,"E1"),sQuery(id+"F0.wireOp",EDGE,"E2.MirrorCS"),sQuery(id+"F0.wireOp",EDGE,"E3"),sQuery(id+"F0.wireOp",EDGE,"E4"),sQuery(id+"F0.wireOp",EDGE,"E5.0.1.0"),sQuery(id+"F0.wireOp",EDGE,"E5.0.1.1"),sQuery(id+"F0.wireOp",EDGE,"E5.0.2.0"),sQuery(id+"F0.wireOp",EDGE,"E5.0.2.1"),sQuery(id+"F0.wireOp",EDGE,"E5.0.3.0"),sQuery(id+"F0.wireOp",EDGE,"E5.0.3.1"),sQuery(id+"F0.wireOp",EDGE,"E5.0.4.0"),sQuery(id+"F0.wireOp",EDGE,"E5.0.4.1"),sQuery(id+"F0.wireOp",EDGE,"E5.0.5.0"),sQuery(id+"F0.wireOp",EDGE,"E5.0.5.1"),sQuery(id+"F0.wireOp",EDGE,"E5.0.6.0"),sQuery(id+"F0.wireOp",EDGE,"E5.0.6.1"),sQuery(id+"F0.wireOp",EDGE,"E5.0.7.0"),sQuery(id+"F0.wireOp",EDGE,"E5.0.7.1"),sQuery(id+"F0.wireOp",EDGE,"E5.0.8.0"),sQuery(id+"F0.wireOp",EDGE,"E5.0.8.1"),sQuery(id+"F0.wireOp",EDGE,"E5.0.9.0"),sQuery(id+"F0.wireOp",EDGE,"E5.0.9.1"),sQuery(id+"F0.wireOp",EDGE,"E5.0.10.0"),sQuery(id+"F0.wireOp",EDGE,"E5.0.10.1"),sQuery(id+"F0.wireOp",EDGE,"E5.0.11.0"),sQuery(id+"F0.wireOp",EDGE,"E5.0.11.1"),sQuery(id+"F0.wireOp",EDGE,"E5.0.12.0"),sQuery(id+"F0.wireOp",EDGE,"E5.0.12.1"),sQuery(id+"F0.wireOp",EDGE,"E5.0.13.0"),sQuery(id+"F0.wireOp",EDGE,"E5.0.13.1"),sQuery(id+"F0.wireOp",EDGE,"E5.0.14.0"),sQuery(id+"F0.wireOp",EDGE,"E5.0.14.1"),sQuery(id+"F0.wireOp",EDGE,"E5.0.15.0"),sQuery(id+"F0.wireOp",EDGE,"E5.0.15.1"),sQuery(id+"F0.wireOp",EDGE,"E5.0.16.0"),sQuery(id+"F0.wireOp",EDGE,"E5.0.16.1"),sQuery(id+"F0.wireOp",EDGE,"E5.0.17.0"),sQuery(id+"F0.wireOp",EDGE,"E5.0.17.1"),sQuery(id+"F0.wireOp",EDGE,"E5.0.18.0"),sQuery(id+"F0.wireOp",EDGE,"E5.0.18.1"),sQuery(id+"F0.wireOp",EDGE,"E8.trimOffspring"),sQuery(id+"F0.wireOp",EDGE,"E9.trimOffspring"),sQuery(id+"F0.wireOp",EDGE,"E10.trimOffspring"),sQuery(id+"F0.wireOp",EDGE,"E11.trimOffspring"),sQuery(id+"F0.wireOp",EDGE,"E12.trimOffspring"),sQuery(id+"F0.wireOp",EDGE,"E13.trimOffspring"),sQuery(id+"F0.wireOp",EDGE,"E14.trimOffspring"),sQuery(id+"F0.wireOp",EDGE,"E15.trimOffspring"),sQuery(id+"F0.wireOp",EDGE,"E16.trimOffspring"),sQuery(id+"F0.wireOp",EDGE,"E17.trimOffspring"),sQuery(id+"F0.wireOp",EDGE,"E18.trimOffspring"),sQuery(id+"F0.wireOp",EDGE,"E19.trimOffspring"),sQuery(id+"F0.wireOp",EDGE,"E20.trimOffspring"),sQuery(id+"F0.wireOp",EDGE,"E21.trimOffspring"),sQuery(id+"F0.wireOp",EDGE,"E22.trimOffspring"),sQuery(id+"F0.wireOp",EDGE,"E23.trimOffspring"),sQuery(id+"F0.wireOp",EDGE,"E24.trimOffspring"),sQuery(id+"F0.wireOp",EDGE,"E25.trimOffspring"),sQuery(id+"F0.wireOp",EDGE,"E26.trimOffspring"),sQuery(id+"F0.wireOp",EDGE,"E27.trimOffspring"),sQuery(id+"F0.wireOp",EDGE,"E28.trimOffspring"),sQuery(id+"F0.wireOp",EDGE,"E29.trimOffspring"),sQuery(id+"F0.wireOp",EDGE,"E30.trimOffspring"),sQuery(id+"F0.wireOp",EDGE,"E31.trimOffspring"),sQuery(id+"F0.wireOp",EDGE,"E32.trimOffspring"),sQuery(id+"F0.wireOp",EDGE,"E33.trimOffspring"),sQuery(id+"F0.wireOp",EDGE,"E34.trimOffspring"),sQuery(id+"F0.wireOp",EDGE,"E35.trimOffspring"),sQuery(id+"F0.wireOp",EDGE,"E36.trimOffspring"),sQuery(id+"F0.wireOp",EDGE,"E37.trimOffspring"),sQuery(id+"F0.wireOp",EDGE,"E38.trimOffspring"),sQuery(id+"F0.wireOp",EDGE,"E39.trimOffspring"),sQuery(id+"F0.wireOp",EDGE,"E41.trimOffspring"),sQuery(id+"F0.wireOp",EDGE,"E42.trimOffspring"),sQuery(id+"F0.wireOp",EDGE,"E43.trimOffspring"),sQuery(id+"F0.wireOp",EDGE,"E45")])],"isStart":true});
            var sketch = newSketch(context, id + "F6", { "sketchPlane" : qUnion([Q0])});
            skLineSegment(sketch, "E53.bottom", {"start": v(-11, 35.5) * mm, "end": v(-10, 35.5) * mm});
            skLineSegment(sketch, "E53.top", {"start": v(-11, 32) * mm, "end": v(-10, 32) * mm});
            skLineSegment(sketch, "E53.left", {"start": v(-11, 35.5) * mm, "end": v(-11, 32) * mm});
            skLineSegment(sketch, "E53.right", {"start": v(-10, 35.5) * mm, "end": v(-10, 32) * mm});
            skLineSegment(sketch, "E54.bottom", {"start": v(9, 31.5) * mm, "end": v(10, 31.5) * mm});
            skLineSegment(sketch, "E54.top", {"start": v(9, 28) * mm, "end": v(10, 28) * mm});
            skLineSegment(sketch, "E54.left", {"start": v(10, 31.5) * mm, "end": v(10, 28) * mm});
            skLineSegment(sketch, "E54.right", {"start": v(9, 31.5) * mm, "end": v(9, 28) * mm});
            skLineSegment(sketch, "E55.0.1.0", {"start": v(-11, 27.5) * mm, "end": v(-11, 24) * mm});
            skLineSegment(sketch, "E55.0.1.1", {"start": v(-10, 27.5) * mm, "end": v(-10, 24) * mm});
            skLineSegment(sketch, "E55.0.1.2", {"start": v(10, 23.5) * mm, "end": v(10, 20) * mm});
            skLineSegment(sketch, "E55.0.1.3", {"start": v(9, 23.5) * mm, "end": v(9, 20) * mm});
            skLineSegment(sketch, "E55.0.1.4", {"start": v(-11, 24) * mm, "end": v(-10, 24) * mm});
            skLineSegment(sketch, "E55.0.1.5", {"start": v(-11, 27.5) * mm, "end": v(-10, 27.5) * mm});
            skLineSegment(sketch, "E55.0.1.6", {"start": v(9, 23.5) * mm, "end": v(10, 23.5) * mm});
            skLineSegment(sketch, "E55.0.1.7", {"start": v(9, 20) * mm, "end": v(10, 20) * mm});
            skLineSegment(sketch, "E55.0.2.0", {"start": v(-11, 19.5) * mm, "end": v(-11, 16) * mm});
            skLineSegment(sketch, "E55.0.2.1", {"start": v(-10, 19.5) * mm, "end": v(-10, 16) * mm});
            skLineSegment(sketch, "E55.0.2.2", {"start": v(10, 15.5) * mm, "end": v(10, 12) * mm});
            skLineSegment(sketch, "E55.0.2.3", {"start": v(9, 15.5) * mm, "end": v(9, 12) * mm});
            skLineSegment(sketch, "E55.0.2.4", {"start": v(-11, 16) * mm, "end": v(-10, 16) * mm});
            skLineSegment(sketch, "E55.0.2.5", {"start": v(-11, 19.5) * mm, "end": v(-10, 19.5) * mm});
            skLineSegment(sketch, "E55.0.2.6", {"start": v(9, 15.5) * mm, "end": v(10, 15.5) * mm});
            skLineSegment(sketch, "E55.0.2.7", {"start": v(9, 12) * mm, "end": v(10, 12) * mm});
            skLineSegment(sketch, "E55.0.3.0", {"start": v(-11, 11.5) * mm, "end": v(-11, 8) * mm});
            skLineSegment(sketch, "E55.0.3.1", {"start": v(-10, 11.5) * mm, "end": v(-10, 8) * mm});
            skLineSegment(sketch, "E55.0.3.2", {"start": v(10, 7.5) * mm, "end": v(10, 4) * mm});
            skLineSegment(sketch, "E55.0.3.3", {"start": v(9, 7.5) * mm, "end": v(9, 4) * mm});
            skLineSegment(sketch, "E55.0.3.4", {"start": v(-11, 8) * mm, "end": v(-10, 8) * mm});
            skLineSegment(sketch, "E55.0.3.5", {"start": v(-11, 11.5) * mm, "end": v(-10, 11.5) * mm});
            skLineSegment(sketch, "E55.0.3.6", {"start": v(9, 7.5) * mm, "end": v(10, 7.5) * mm});
            skLineSegment(sketch, "E55.0.3.7", {"start": v(9, 4) * mm, "end": v(10, 4) * mm});
            skLineSegment(sketch, "E55.0.4.0", {"start": v(-11, 3.5) * mm, "end": v(-11, 0) * mm});
            skLineSegment(sketch, "E55.0.4.1", {"start": v(-10, 3.5) * mm, "end": v(-10, 0) * mm});
            skLineSegment(sketch, "E55.0.4.2", {"start": v(10, -0.5) * mm, "end": v(10, -4) * mm});
            skLineSegment(sketch, "E55.0.4.3", {"start": v(9, -0.5) * mm, "end": v(9, -4) * mm});
            skLineSegment(sketch, "E55.0.4.4", {"start": v(-11, 0) * mm, "end": v(-10, 0) * mm});
            skLineSegment(sketch, "E55.0.4.5", {"start": v(-11, 3.5) * mm, "end": v(-10, 3.5) * mm});
            skLineSegment(sketch, "E55.0.4.6", {"start": v(9, -0.5) * mm, "end": v(10, -0.5) * mm});
            skLineSegment(sketch, "E55.0.4.7", {"start": v(9, -4) * mm, "end": v(10, -4) * mm});
            skLineSegment(sketch, "E55.0.5.0", {"start": v(-11, -4.5) * mm, "end": v(-11, -8) * mm});
            skLineSegment(sketch, "E55.0.5.1", {"start": v(-10, -4.5) * mm, "end": v(-10, -8) * mm});
            skLineSegment(sketch, "E55.0.5.2", {"start": v(10, -8.5) * mm, "end": v(10, -12) * mm});
            skLineSegment(sketch, "E55.0.5.3", {"start": v(9, -8.5) * mm, "end": v(9, -12) * mm});
            skLineSegment(sketch, "E55.0.5.4", {"start": v(-11, -8) * mm, "end": v(-10, -8) * mm});
            skLineSegment(sketch, "E55.0.5.5", {"start": v(-11, -4.5) * mm, "end": v(-10, -4.5) * mm});
            skLineSegment(sketch, "E55.0.5.6", {"start": v(9, -8.5) * mm, "end": v(10, -8.5) * mm});
            skLineSegment(sketch, "E55.0.5.7", {"start": v(9, -12) * mm, "end": v(10, -12) * mm});
            skLineSegment(sketch, "E55.0.6.0", {"start": v(-11, -12.5) * mm, "end": v(-11, -16) * mm});
            skLineSegment(sketch, "E55.0.6.1", {"start": v(-10, -12.5) * mm, "end": v(-10, -16) * mm});
            skLineSegment(sketch, "E55.0.6.2", {"start": v(10, -16.5) * mm, "end": v(10, -20) * mm});
            skLineSegment(sketch, "E55.0.6.3", {"start": v(9, -16.5) * mm, "end": v(9, -20) * mm});
            skLineSegment(sketch, "E55.0.6.4", {"start": v(-11, -16) * mm, "end": v(-10, -16) * mm});
            skLineSegment(sketch, "E55.0.6.5", {"start": v(-11, -12.5) * mm, "end": v(-10, -12.5) * mm});
            skLineSegment(sketch, "E55.0.6.6", {"start": v(9, -16.5) * mm, "end": v(10, -16.5) * mm});
            skLineSegment(sketch, "E55.0.6.7", {"start": v(9, -20) * mm, "end": v(10, -20) * mm});
            skLineSegment(sketch, "E55.0.7.0", {"start": v(-11, -20.5) * mm, "end": v(-11, -24) * mm});
            skLineSegment(sketch, "E55.0.7.1", {"start": v(-10, -20.5) * mm, "end": v(-10, -24) * mm});
            skLineSegment(sketch, "E55.0.7.2", {"start": v(10, -24.5) * mm, "end": v(10, -28) * mm});
            skLineSegment(sketch, "E55.0.7.3", {"start": v(9, -24.5) * mm, "end": v(9, -28) * mm});
            skLineSegment(sketch, "E55.0.7.4", {"start": v(-11, -24) * mm, "end": v(-10, -24) * mm});
            skLineSegment(sketch, "E55.0.7.5", {"start": v(-11, -20.5) * mm, "end": v(-10, -20.5) * mm});
            skLineSegment(sketch, "E55.0.7.6", {"start": v(9, -24.5) * mm, "end": v(10, -24.5) * mm});
            skLineSegment(sketch, "E55.0.7.7", {"start": v(9, -28) * mm, "end": v(10, -28) * mm});
            skLineSegment(sketch, "E55.0.8.0", {"start": v(-11, -28.5) * mm, "end": v(-11, -32) * mm});
            skLineSegment(sketch, "E55.0.8.1", {"start": v(-10, -28.5) * mm, "end": v(-10, -32) * mm});
            skLineSegment(sketch, "E55.0.8.2", {"start": v(10, -32.5) * mm, "end": v(10, -36) * mm});
            skLineSegment(sketch, "E55.0.8.3", {"start": v(9, -32.5) * mm, "end": v(9, -36) * mm});
            skLineSegment(sketch, "E55.0.8.4", {"start": v(-11, -32) * mm, "end": v(-10, -32) * mm});
            skLineSegment(sketch, "E55.0.8.5", {"start": v(-11, -28.5) * mm, "end": v(-10, -28.5) * mm});
            skLineSegment(sketch, "E55.0.8.6", {"start": v(9, -32.5) * mm, "end": v(10, -32.5) * mm});
            skLineSegment(sketch, "E55.0.8.7", {"start": v(9, -36) * mm, "end": v(10, -36) * mm});
            skLineSegment(sketch, "E55.direction1", {"start": v(-11, 32) * mm, "end": v(14, 32) * mm, "construction": true});
            skLineSegment(sketch, "E55.direction2", {"start": v(-11, 32) * mm, "end": v(-11, 24) * mm, "construction": true});
            skSolve(sketch);
        }
        {
            var Q0;
            Q0 = qSketchRegion(id + "F6", true);
            extrude(context, id + "F7", {"entities" : qUnion([Q0]), "operationType" : NewBodyOperationType.REMOVE, "oppositeDirection" : true, "depth" : 1.2 * mm});
        }
    });
